# Revit family: BE_66157_de_DE
name_source: partatom
category: Leuchten
units: mm (PartAtom-declared; Revit-internal decimal feet)

## family parameters
Basisbauteil = Fläche
Beim Laden mit Abzugskörper schneiden = Ja
Bemaßung runder Anschluss = Durchmesser verwenden
Gemeinsam genutzt = Nein
Lichtquelle = Ja
Raumberechnungspunkt = Ja
Teiletyp = Normal

## types (4) — shared parameters
AC/DC = AC/DC
Aktualisierung = 2022-05-19T04:00:07
BEGA_Dummy = Nein
BEGA_IES = Ja
BEGA_Intern = Ja
BEGA_Intern_Konstruktion = Ja
BEGA_Intern_an = Ja
BEGA_Intern_aus = Ja
Befestigungsabstand = 70 mm
Befestigungsbohrung = Ø 4,8 mm
Beschreibung = Kompakttiefstrahler
Beschreibung_Sonderanfertigung = Hier können Sie Informationen zur Sonderanfertigung eintragen.
CE_Konformität = ja
Energieeffizienzklasse = LED A++ - A
Farbfilter = 16777215
Farbtemperaturverschiebung bei Dämpfen der Lampe = <Keine Auswahl>
Farbwiedergabeindex = CRI > 80
Frequenz = 0/50-60 Hz
Gewicht = 0.85 kg
Hersteller = BEGA
Lampe = LED 3 W
Lastklassifizierung = Beleuchtung
Lebensdauerkriterien = L70B50 @ 25 °C = 200000 h
Logo = BEGA_Logo.png
Material_03 = BEGA_Oberfläche_Weiss_matt
Material_06 = BEGA_Oberfläche_Edelstahl_gebürstet
Material_09 = BEGA_Glas_klar
Material_15 = BEGA_Leuchtmedium_matt
Material_19 = BEGA_Dummy_matt
Neigungswinkel = 0.00°
Produktdatenblatt = https://cdn.bega.com
Scheinlast = 0 VA
Schutzart = IP 65
Schutzklasse = I
Sonderanfertigung = Nein
Spannung = 240 V
Typenbild = 66157.png
URL = https://www.bega.com
Umgebungstemperatur = 25 °C
zero-valued in all types: Vorgabe-Ansicht

## per-type parameters (varying)
| type | Bestellnummer | Datei für fotometrisches Netz | Farbtemperatur | LED_Modulbezeichnung | Lampenlichtstrom | Leuchtenlichtstrom | M_G | M_W | Modell |
| BEGA_66157_Grafit_K4 | 66157K4 | BE_66157K4.IES | 4000 K | LED-0591/840 | 580 lm | 440 lm | Ja | Nein | 66157K4 |
| BEGA_66157_Weiß_K3 | 66157WK3 | BE_66157K3.IES | 3000 K | LED-0591/830 | 560 lm | 424 lm | Nein | Ja | 66157WK3 |
| BEGA_66157_Grafit_K3 | 66157K3 | BE_66157K3.IES | 3000 K | LED-0591/830 | 560 lm | 424 lm | Ja | Nein | 66157K3 |
| BEGA_66157_Weiß_K4 | 66157WK4 | BE_66157K4.IES | 4000 K | LED-0591/840 | 580 lm | 440 lm | Nein | Ja | 66157WK4 |
